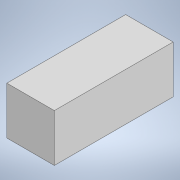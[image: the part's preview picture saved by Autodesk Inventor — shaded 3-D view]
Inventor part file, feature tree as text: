
AUTODESK INVENTOR PART (.ipt)
format: ipt  version: 2022 (Build 260153000, 153)  size: 94,720 bytes
history: native  units: mm
features: extrude x1, sketch x1
ambient origin geometry x8: Origin, YZ Plane, XZ Plane, XY Plane, X Axis, Y Axis, Z Axis, Center Point
bodies: Solid1 (feature_tree)
feature tree (2):
  extrude  "Extrusion1"  Depth=20.0mm
  sketch  "Sketch1"  dims[d0=20.0mm d1=20.0mm d2=10.0mm d3=10.0mm d4=50.0mm d5=0.0mm]
